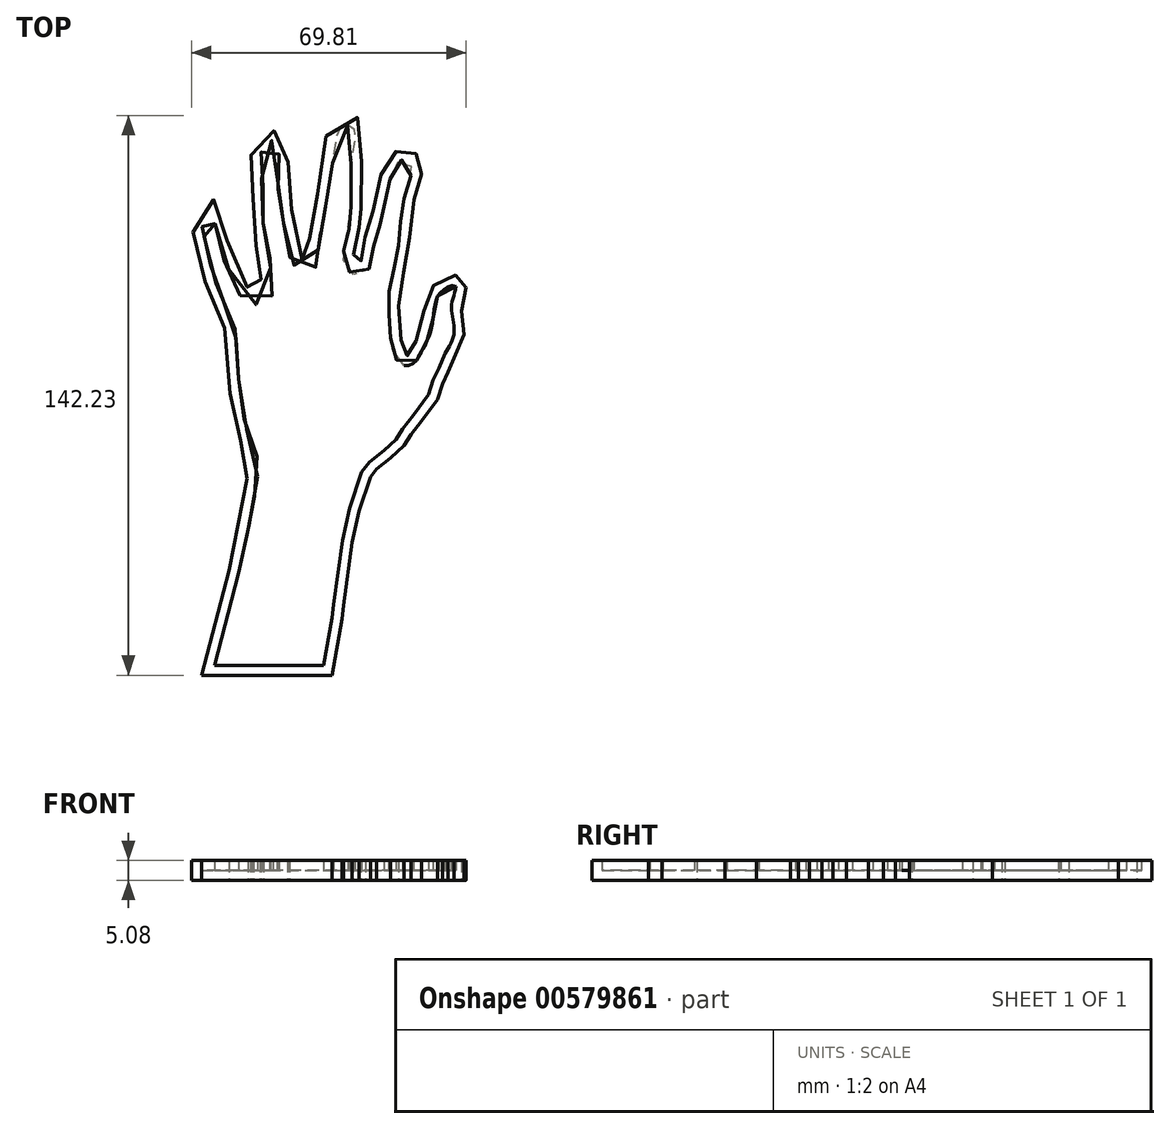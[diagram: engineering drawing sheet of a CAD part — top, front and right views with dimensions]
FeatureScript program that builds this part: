
annotation { "Feature Type Name" : "Feature", "Feature Type Description" : "" }
export const myFeature = defineFeature(function(context is Context, id is Id, definition is map)
    precondition{}
    {
        {
            var Q0;
            Q0=qCreatedBy(makeId("Top.planeOp"),FACE);
            var sketch = newSketch(context, id + "F0", { "sketchPlane" : qUnion([Q0])});
            skLineSegment(sketch, "E0", {"start": v(-75.45, -50.39) * mm, "end": v(-82.4, -77) * mm});
            skLineSegment(sketch, "E1", {"start": v(-82.4, -77) * mm, "end": v(-49.22, -77) * mm});
            skLineSegment(sketch, "E2", {"start": v(-49.22, -77) * mm, "end": v(-46.69, -62.74) * mm});
            skLineSegment(sketch, "E3", {"start": v(-46.69, -62.74) * mm, "end": v(-46.32, -59.31) * mm});
            skLineSegment(sketch, "E4", {"start": v(-46.32, -59.31) * mm, "end": v(-44.12, -43.24) * mm});
            skLineSegment(sketch, "E5", {"start": v(-44.12, -43.24) * mm, "end": v(-42.35, -35.27) * mm});
            skLineSegment(sketch, "E6", {"start": v(-42.35, -35.27) * mm, "end": v(-39.49, -26.58) * mm});
            skLineSegment(sketch, "E7", {"start": v(-39.49, -26.58) * mm, "end": v(-37.92, -24.57) * mm});
            skLineSegment(sketch, "E8", {"start": v(-37.92, -24.57) * mm, "end": v(-34.34, -21.81) * mm});
            skLineSegment(sketch, "E9", {"start": v(-34.34, -21.81) * mm, "end": v(-31, -18.67) * mm});
            skLineSegment(sketch, "E10", {"start": v(-31, -18.67) * mm, "end": v(-29.2, -15.87) * mm});
            skLineSegment(sketch, "E11", {"start": v(-29.2, -15.87) * mm, "end": v(-26.5, -12.37) * mm});
            skLineSegment(sketch, "E12", {"start": v(-26.5, -12.37) * mm, "end": v(-22.4, -6.88) * mm});
            skLineSegment(sketch, "E13", {"start": v(-22.4, -6.88) * mm, "end": v(-21.18, -2.96) * mm});
            skLineSegment(sketch, "E14", {"start": v(-21.18, -2.96) * mm, "end": v(-19.75, 0) * mm});
            skLineSegment(sketch, "E15", {"start": v(-19.75, 0) * mm, "end": v(-18.3, 3.6) * mm});
            skPoint(sketch, "E16.20.internal.snap0", {"position": v(-27.85, -14.12) * mm});
            skFitSpline(sketch, "E16", {"points": [v(-18.3, 3.6) * mm, v(-15.94, 8.34) * mm, v(-15.84, 12.96) * mm, v(-16.28, 17) * mm, v(-15.16, 21.46) * mm, v(-15.84, 23.56) * mm, v(-18.3, 24.66) * mm, v(-22.58, 22.86) * mm, v(-25.31, 18.89) * mm, v(-26.6, 11.15) * mm, v(-29.03, 5.95) * mm, v(-29.75, 4.67) * mm, v(-30.4, 4.19) * mm, v(-31.23, 5.9) * mm, v(-31.96, 10.62) * mm, v(-32.1, 21.47) * mm, v(-30.22, 28.69) * mm, v(-28.96, 41) * mm, v(-27.22, 47.6) * mm, v(-26.42, 52.17) * mm, v(-27.85, 55.49) * mm, v(-30.57, 56.64) * mm, v(-34.32, 55.13) * mm, v(-37.2, 48.64) * mm, v(-39.44, 38.45) * mm, v(-40.95, 34.02) * mm, v(-41.58, 29.56) * mm, v(-42.5, 27.08) * mm, v(-43.83, 29.18) * mm, v(-42.34, 35.69) * mm, v(-42.57, 38.37) * mm, v(-41.88, 41.62) * mm], "startDerivative": vector(83.5, 133.62) * mm, "endDerivative": vector(39.73, 125.12) * mm});
            skFitSpline(sketch, "E17", {"points": [v(-41.88, 41.62) * mm, v(-41.88, 45.77) * mm, v(-41.88, 52.64) * mm, v(-40.85, 58.43) * mm, v(-41.88, 64) * mm, v(-46.27, 65.1) * mm, v(-49.74, 62.8) * mm, v(-51.07, 57.46) * mm, v(-52.55, 47.94) * mm, v(-53.72, 41) * mm, v(-54.64, 36.34) * mm, v(-55.22, 32.07) * mm, v(-55.44, 29.2) * mm, v(-55.66, 27.87) * mm, v(-56.96, 28.83) * mm, v(-58.86, 37.07) * mm, v(-59.54, 41.62) * mm, v(-60.44, 47.38) * mm, v(-60.39, 53.38) * mm, v(-60.2, 58.22) * mm, v(-62.1, 60.6) * mm, v(-65.73, 61.37) * mm, v(-68.7, 59.38) * mm, v(-69.77, 56.03) * mm, v(-69.8, 49.66) * mm, v(-69.15, 45.74) * mm, v(-69.65, 41.62) * mm, v(-68.78, 34.57) * mm, v(-68.2, 30.72) * mm, v(-67.3, 27.48) * mm, v(-67.52, 24.68) * mm, v(-66.79, 22.02) * mm, v(-67.06, 20.17) * mm, v(-69.62, 20.04) * mm, v(-71.74, 24.17) * mm, v(-75.04, 30.94) * mm, v(-76.34, 36.14) * mm, v(-77.15, 41.62) * mm, v(-80.36, 44.12) * mm, v(-84.44, 41.62) * mm, v(-84.33, 34.45) * mm, v(-82.75, 27.23) * mm, v(-81.08, 21.73) * mm, v(-77.77, 13.99) * mm, v(-76.4, 10.36) * mm, v(-75.45, -2.69) * mm, v(-74.6, -9) * mm, v(-73.1, -16.06) * mm, v(-71.67, -18.74) * mm, v(-70.68, -22.64) * mm, v(-70.85, -27.55) * mm, v(-75.45, -50.39) * mm], "startDerivative": vector(3.98, 215.87) * mm, "endDerivative": vector(-140.37, -647.37) * mm});
            skSolve(sketch);
        }
        {
            var Q0;
            Q0 = qSketchRegion(id + "F0", true);
            extrude(context, id + "F1", {"entities" : qUnion([Q0]), "depth" : 5.08 * mm, "offsetDistance" : 25.4 * mm});
        }
        {
            var Q0;
            Q0=makeQuery(id+"F1.opExtrude","CAP_FACE",FACE,{"disambiguationData":[OSD([sQuery(id+"F0.wireOp",EDGE,"E0"),sQuery(id+"F0.wireOp",EDGE,"E1"),sQuery(id+"F0.wireOp",EDGE,"E2"),sQuery(id+"F0.wireOp",EDGE,"E3"),sQuery(id+"F0.wireOp",EDGE,"E4"),sQuery(id+"F0.wireOp",EDGE,"E5"),sQuery(id+"F0.wireOp",EDGE,"E6"),sQuery(id+"F0.wireOp",EDGE,"E7"),sQuery(id+"F0.wireOp",EDGE,"E8"),sQuery(id+"F0.wireOp",EDGE,"E9"),sQuery(id+"F0.wireOp",EDGE,"E10"),sQuery(id+"F0.wireOp",EDGE,"E11"),sQuery(id+"F0.wireOp",EDGE,"E12"),sQuery(id+"F0.wireOp",EDGE,"E13"),sQuery(id+"F0.wireOp",EDGE,"E14"),sQuery(id+"F0.wireOp",EDGE,"E15"),sQuery(id+"F0.wireOp",EDGE,"E16"),sQuery(id+"F0.wireOp",EDGE,"E17")])],"isStart":false});
            shell(context, id + "F2", {"entities" : qUnion([Q0]), "thickness" : 2.54 * mm});
        }
    });
